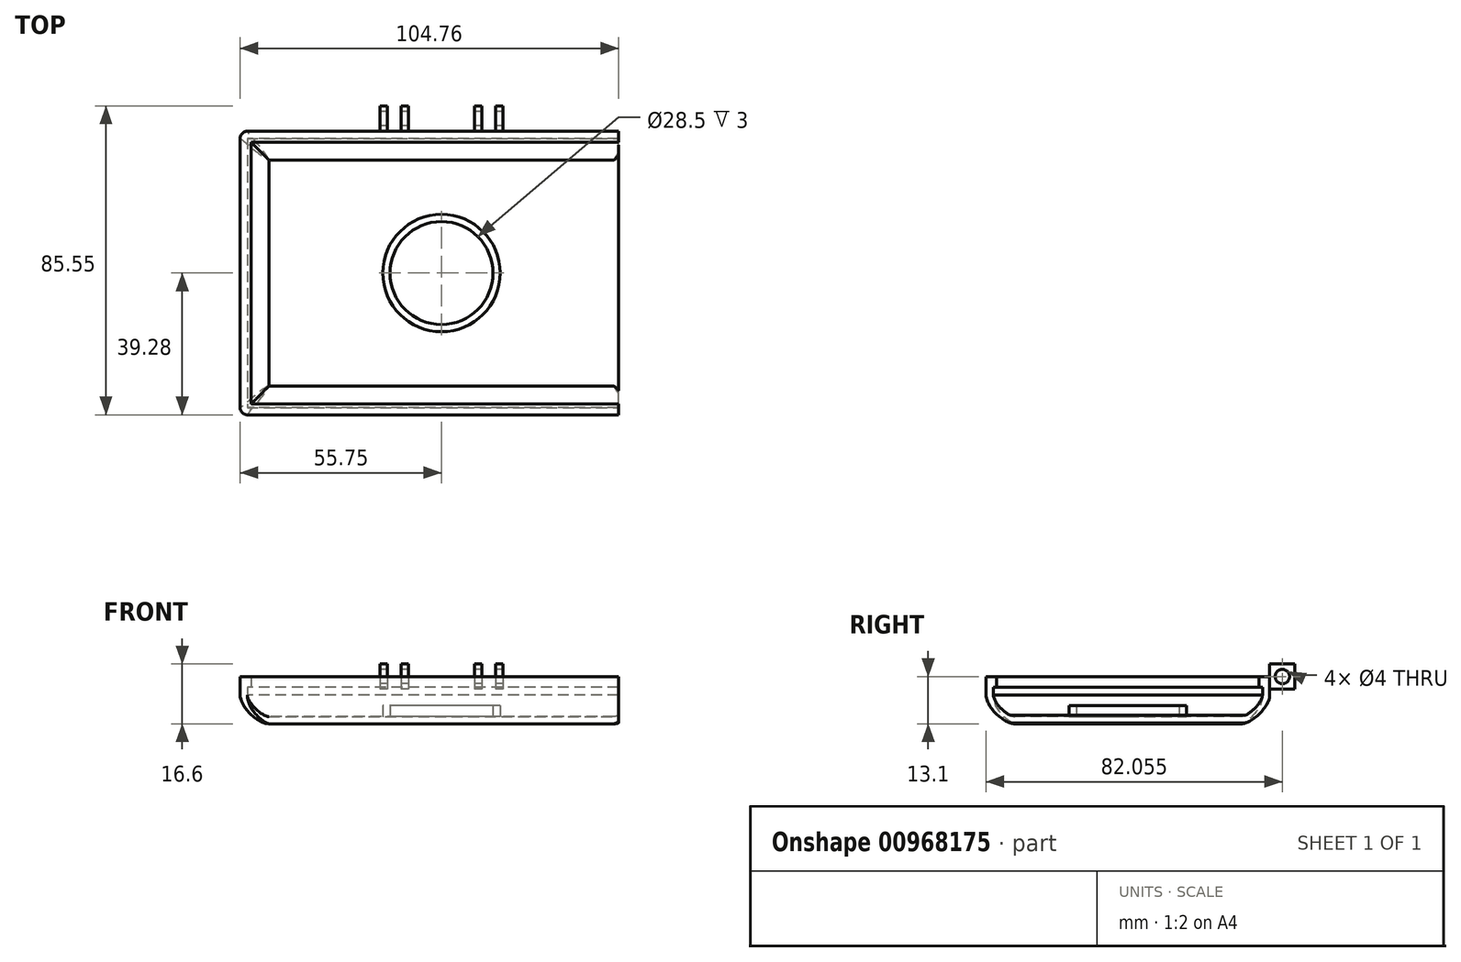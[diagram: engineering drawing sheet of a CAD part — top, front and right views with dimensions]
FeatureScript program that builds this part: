
annotation { "Feature Type Name" : "Feature", "Feature Type Description" : "" }
export const myFeature = defineFeature(function(context is Context, id is Id, definition is map)
    precondition{}
    {
        {
            var Q0;
            Q0=qCreatedBy(makeId("Top.planeOp"),FACE);
            var sketch = newSketch(context, id + "F0", { "sketchPlane" : qUnion([Q0])});
            skLineSegment(sketch, "E0.bottom", {"start": v(55.75, 39.28) * mm, "end": v(-55.75, 39.28) * mm});
            skLineSegment(sketch, "E0.top", {"start": v(55.75, -39.28) * mm, "end": v(-55.75, -39.28) * mm});
            skLineSegment(sketch, "E0.left", {"start": v(55.75, 39.28) * mm, "end": v(55.75, -39.28) * mm});
            skLineSegment(sketch, "E0.right", {"start": v(-55.75, 39.28) * mm, "end": v(-55.75, -39.28) * mm});
            skPoint(sketch, "E0.middle", {"position": v(0, 0) * mm});
            skSolve(sketch);
        }
        {
            var Q0;
            Q0=makeQuery(id+"F0.imprint","IMPRINT",FACE,{"disambiguationData":[TD([[makeQuery(id+"F0.imprint","IMPRINT",EDGE,{"derivedFrom":sQuery(id+"F0.wireOp",EDGE,"E0.bottom")}),1.0]])]});
            extrude(context, id + "F1", {"entities" : qUnion([Q0]), "oppositeDirection" : true, "depth" : 9.6 * mm, "offsetDistance" : 25 * mm});
        }
        {
            var Q0;
            Q0=makeQuery(id+"F1.opExtrude","CAP_FACE",FACE,{"disambiguationData":[OSD([sQuery(id+"F0.wireOp",EDGE,"E0.bottom"),sQuery(id+"F0.wireOp",EDGE,"E0.top"),sQuery(id+"F0.wireOp",EDGE,"E0.left"),sQuery(id+"F0.wireOp",EDGE,"E0.right")])],"isStart":false});
            fillet(context, id + "F2", {"entities" : qUnion([Q0]), "radius" : 8 * mm, "tangentPropagation" : true, "rho" : .3, "crossSection" : FilletCrossSection.CONIC, "allowEdgeOverflow" : false});
        }
        {
            var Q0;
            Q0=makeQuery(id+"F2.opFillet","BLEND_EDGE",EDGE,{"blendedFrom":[makeQuery(id+"F1.opExtrude","CAP_EDGE",EDGE,{"disambiguationData":[OSD([sQuery(id+"F0.wireOp",EDGE,"E0.top")])],"isStart":false}),makeQuery(id+"F1.opExtrude","CAP_EDGE",EDGE,{"disambiguationData":[OSD([sQuery(id+"F0.wireOp",EDGE,"E0.right")])],"isStart":false})],"blendedInto":[]});
            var Q1;
            Q1=makeQuery(id+"F2.opFillet","BLEND_EDGE",EDGE,{"blendedFrom":[makeQuery(id+"F1.opExtrude","CAP_EDGE",EDGE,{"disambiguationData":[OSD([sQuery(id+"F0.wireOp",EDGE,"E0.top")])],"isStart":false}),makeQuery(id+"F1.opExtrude","CAP_EDGE",EDGE,{"disambiguationData":[OSD([sQuery(id+"F0.wireOp",EDGE,"E0.left")])],"isStart":false})],"blendedInto":[]});
            var Q2;
            Q2=makeQuery(id+"F2.opFillet","BLEND_EDGE",EDGE,{"blendedFrom":[makeQuery(id+"F1.opExtrude","CAP_EDGE",EDGE,{"disambiguationData":[OSD([sQuery(id+"F0.wireOp",EDGE,"E0.bottom")])],"isStart":false}),makeQuery(id+"F1.opExtrude","CAP_EDGE",EDGE,{"disambiguationData":[OSD([sQuery(id+"F0.wireOp",EDGE,"E0.left")])],"isStart":false})],"blendedInto":[]});
            var Q3;
            Q3=makeQuery(id+"F2.opFillet","BLEND_EDGE",EDGE,{"blendedFrom":[makeQuery(id+"F1.opExtrude","CAP_EDGE",EDGE,{"disambiguationData":[OSD([sQuery(id+"F0.wireOp",EDGE,"E0.bottom")])],"isStart":false}),makeQuery(id+"F1.opExtrude","CAP_EDGE",EDGE,{"disambiguationData":[OSD([sQuery(id+"F0.wireOp",EDGE,"E0.right")])],"isStart":false})],"blendedInto":[]});
            fillet(context, id + "F3", {"entities" : qUnion([Q0, Q1, Q2, Q3]), "radius" : 2 * mm, "tangentPropagation" : true, "allowEdgeOverflow" : false});
        }
        {
            var Q0;
            Q0=makeQuery(id+"F1.opExtrude","CAP_FACE",FACE,{"disambiguationData":[OSD([sQuery(id+"F0.wireOp",EDGE,"E0.bottom"),sQuery(id+"F0.wireOp",EDGE,"E0.top"),sQuery(id+"F0.wireOp",EDGE,"E0.left"),sQuery(id+"F0.wireOp",EDGE,"E0.right")])],"isStart":true});
            shell(context, id + "F4", {"entities" : qUnion([Q0]), "thickness" : 2 * mm});
        }
        {
            var Q0;
            Q0=qCreatedBy(makeId("Top.planeOp"),FACE);
            var sketch = newSketch(context, id + "F5", { "sketchPlane" : qUnion([Q0])});
            skLineSegment(sketch, "E1.0", {"start": v(-53.75, 37.28) * mm, "end": v(-53.75, -37.28) * mm});
            skLineSegment(sketch, "E2.0", {"start": v(53.75, 37.28) * mm, "end": v(-53.75, 37.28) * mm});
            skLineSegment(sketch, "E3.0", {"start": v(53.75, 37.28) * mm, "end": v(53.75, -37.28) * mm});
            skLineSegment(sketch, "E4.0", {"start": v(53.75, -37.28) * mm, "end": v(-53.75, -37.28) * mm});
            skLineSegment(sketch, "E5.0", {"start": v(-55.75, 37.28) * mm, "end": v(-55.75, -37.28) * mm});
            skLineSegment(sketch, "E6.0.0", {"start": v(-53.75, -39.28) * mm, "end": v(53.75, -39.28) * mm});
            skArc(sketch, "E6.0.1", {"start": v(53.75, -39.28) * mm, "mid": v(55.16, -38.69) * mm, "end": v(55.75, -37.28) * mm});
            skLineSegment(sketch, "E6.0.2", {"start": v(55.75, -37.28) * mm, "end": v(55.75, 37.28) * mm});
            skArc(sketch, "E6.0.3", {"start": v(55.75, 37.28) * mm, "mid": v(55.16, 38.69) * mm, "end": v(53.75, 39.28) * mm});
            skLineSegment(sketch, "E6.0.4", {"start": v(53.75, 39.28) * mm, "end": v(-53.75, 39.28) * mm});
            skArc(sketch, "E6.0.5", {"start": v(-53.75, 39.28) * mm, "mid": v(-55.16, 38.69) * mm, "end": v(-55.75, 37.28) * mm});
            skArc(sketch, "E6.0.7", {"start": v(-55.75, -37.28) * mm, "mid": v(-55.16, -38.69) * mm, "end": v(-53.75, -39.28) * mm});
            skSolve(sketch);
        }
        {
            var Q0;
            Q0 = qSketchRegion(id + "F5", true);
            extrude(context, id + "F6", {"entities" : qUnion([Q0]), "operationType" : NewBodyOperationType.ADD, "depth" : .5 * mm, "offsetDistance" : 25 * mm});
        }
        {
            var Q0;
            Q0=makeQuery(id+"F6.opExtrude","CAP_FACE",FACE,{"disambiguationData":[OSD([sQuery(id+"F5.wireOp",EDGE,"E1.0"),sQuery(id+"F5.wireOp",EDGE,"E2.0"),sQuery(id+"F5.wireOp",EDGE,"E3.0"),sQuery(id+"F5.wireOp",EDGE,"E4.0"),sQuery(id+"F5.wireOp",EDGE,"E6.0.0"),sQuery(id+"F5.wireOp",EDGE,"E6.0.1"),sQuery(id+"F5.wireOp",EDGE,"E6.0.2"),sQuery(id+"F5.wireOp",EDGE,"E6.0.3"),sQuery(id+"F5.wireOp",EDGE,"E6.0.4"),sQuery(id+"F5.wireOp",EDGE,"E6.0.5"),sQuery(id+"F5.wireOp",EDGE,"E5.0"),sQuery(id+"F5.wireOp",EDGE,"E6.0.7")])],"isStart":false});
            var sketch = newSketch(context, id + "F7", { "sketchPlane" : qUnion([Q0])});
            skLineSegment(sketch, "E7.0", {"start": v(52.75, 36.27) * mm, "end": v(-52.75, 36.27) * mm});
            skLineSegment(sketch, "E7.1", {"start": v(52.75, 36.27) * mm, "end": v(52.75, -36.27) * mm});
            skLineSegment(sketch, "E7.2", {"start": v(52.75, -36.27) * mm, "end": v(-52.75, -36.27) * mm});
            skLineSegment(sketch, "E7.3", {"start": v(-52.75, 36.27) * mm, "end": v(-52.75, -36.27) * mm});
            skLineSegment(sketch, "E8.0", {"start": v(53.75, 39.28) * mm, "end": v(-53.75, 39.28) * mm});
            skPoint(sketch, "E9.0", {"position": v(55.16, 38.69) * mm});
            skArc(sketch, "E10.0", {"start": v(55.75, 37.28) * mm, "mid": v(55.16, 38.69) * mm, "end": v(53.75, 39.28) * mm});
            skLineSegment(sketch, "E11.0", {"start": v(55.75, -37.28) * mm, "end": v(55.75, 37.28) * mm});
            skArc(sketch, "E12.0", {"start": v(53.75, -39.28) * mm, "mid": v(55.16, -38.69) * mm, "end": v(55.75, -37.28) * mm});
            skLineSegment(sketch, "E13.0", {"start": v(-53.75, -39.28) * mm, "end": v(53.75, -39.28) * mm});
            skArc(sketch, "E14.0", {"start": v(-55.75, -37.28) * mm, "mid": v(-55.16, -38.69) * mm, "end": v(-53.75, -39.28) * mm});
            skLineSegment(sketch, "E15.0", {"start": v(-55.75, 37.28) * mm, "end": v(-55.75, -37.28) * mm});
            skArc(sketch, "E16.0", {"start": v(-53.75, 39.28) * mm, "mid": v(-55.16, 38.69) * mm, "end": v(-55.75, 37.28) * mm});
            skSolve(sketch);
        }
        {
            var Q0;
            Q0 = qSketchRegion(id + "F7", true);
            extrude(context, id + "F8", {"entities" : qUnion([Q0]), "operationType" : NewBodyOperationType.ADD, "depth" : 3 * mm, "offsetDistance" : 25 * mm});
        }
        {
            var Q0;
            Q0=makeQuery(id+"F4.opShell","OFFSET_FACE",FACE,{"disambiguationData":[OSD([sQuery(id+"F0.wireOp",EDGE,"E0.bottom"),sQuery(id+"F0.wireOp",EDGE,"E0.top"),sQuery(id+"F0.wireOp",EDGE,"E0.left"),sQuery(id+"F0.wireOp",EDGE,"E0.right")])]});
            var sketch = newSketch(context, id + "F9", { "sketchPlane" : qUnion([Q0])});
            skCircle(sketch, "E17", {"center": v(0, 0) * mm, "radius": 14.25 * mm});
            skCircle(sketch, "E18.0", {"center": v(0, 0) * mm, "radius": 16.25 * mm});
            skSolve(sketch);
        }
        {
            var Q0;
            Q0 = qSketchRegion(id + "F9", true);
            extrude(context, id + "F10", {"entities" : qUnion([Q0]), "operationType" : NewBodyOperationType.ADD, "depth" : 3 * mm, "offsetDistance" : 25 * mm});
        }
        {
            var Q0;
            Q0=qCreatedBy(makeId("Top.planeOp"),FACE);
            var sketch = newSketch(context, id + "F11", { "sketchPlane" : qUnion([Q0])});
            skLineSegment(sketch, "E19.bottom", {"start": v(49, 46.46) * mm, "end": v(61.97, 46.46) * mm});
            skLineSegment(sketch, "E19.top", {"start": v(49, -47.3) * mm, "end": v(61.97, -47.3) * mm});
            skLineSegment(sketch, "E19.left", {"start": v(49, 46.46) * mm, "end": v(49, -47.3) * mm});
            skLineSegment(sketch, "E19.right", {"start": v(61.97, 46.46) * mm, "end": v(61.97, -47.3) * mm});
            skSolve(sketch);
        }
        {
            var Q0;
            Q0 = qSketchRegion(id + "F11", true);
            extrude(context, id + "F12", {"entities" : qUnion([Q0]), "operationType" : NewBodyOperationType.REMOVE, "endBound" : BoundingType.SYMMETRIC, "oppositeDirection" : true, "depth" : 25 * mm, "offsetDistance" : 25 * mm});
        }
        {
            var Q0;
            Q0=makeQuery(id+"F8.opExtrude","CAP_FACE",FACE,{"disambiguationData":[OSD([sQuery(id+"F7.wireOp",EDGE,"E7.0"),sQuery(id+"F7.wireOp",EDGE,"E7.1"),sQuery(id+"F7.wireOp",EDGE,"E7.2"),sQuery(id+"F7.wireOp",EDGE,"E7.3"),sQuery(id+"F7.wireOp",EDGE,"E8.0"),sQuery(id+"F7.wireOp",EDGE,"E10.0"),sQuery(id+"F7.wireOp",EDGE,"E11.0"),sQuery(id+"F7.wireOp",EDGE,"E12.0"),sQuery(id+"F7.wireOp",EDGE,"E13.0"),sQuery(id+"F7.wireOp",EDGE,"E14.0"),sQuery(id+"F7.wireOp",EDGE,"E15.0"),sQuery(id+"F7.wireOp",EDGE,"E16.0")])],"isStart":false});
            var sketch = newSketch(context, id + "F13", { "sketchPlane" : qUnion([Q0])});
            skLineSegment(sketch, "E20.0", {"start": v(54.25, 39.28) * mm, "end": v(-53.75, 39.28) * mm, "construction": true});
            skLineSegment(sketch, "E21.bottom", {"start": v(-17, 39.28) * mm, "end": v(-15, 39.28) * mm});
            skLineSegment(sketch, "E21.top", {"start": v(-17, 46.27) * mm, "end": v(-15, 46.27) * mm});
            skLineSegment(sketch, "E21.left", {"start": v(-17, 39.28) * mm, "end": v(-17, 46.27) * mm});
            skLineSegment(sketch, "E21.right", {"start": v(-15, 39.28) * mm, "end": v(-15, 46.27) * mm});
            skLineSegment(sketch, "E22.1.0.0", {"start": v(-9.2, 39.28) * mm, "end": v(-9.2, 46.27) * mm});
            skLineSegment(sketch, "E22.1.0.1", {"start": v(-11.2, 46.27) * mm, "end": v(-9.2, 46.27) * mm});
            skLineSegment(sketch, "E22.1.0.2", {"start": v(-11.2, 39.28) * mm, "end": v(-9.2, 39.28) * mm});
            skLineSegment(sketch, "E22.1.0.3", {"start": v(-11.2, 39.28) * mm, "end": v(-11.2, 46.27) * mm});
            skLineSegment(sketch, "E22.direction1", {"start": v(-17, 39.28) * mm, "end": v(-11.2, 39.28) * mm, "construction": true});
            skLineSegment(sketch, "E23.MirrorCS", {"start": v(17, 39.28) * mm, "end": v(11.2, 39.28) * mm, "construction": true});
            skLineSegment(sketch, "E24.MirrorCS", {"start": v(-54.25, 39.28) * mm, "end": v(53.75, 39.28) * mm, "construction": true});
            skLineSegment(sketch, "E25.MirrorCS", {"start": v(17, 39.28) * mm, "end": v(15, 39.28) * mm});
            skLineSegment(sketch, "E26.MirrorCS", {"start": v(17, 46.27) * mm, "end": v(15, 46.27) * mm});
            skLineSegment(sketch, "E27.MirrorCS", {"start": v(9.2, 39.28) * mm, "end": v(9.2, 46.27) * mm});
            skLineSegment(sketch, "E28.MirrorCS", {"start": v(15, 39.28) * mm, "end": v(15, 46.27) * mm});
            skLineSegment(sketch, "E29.MirrorCS", {"start": v(11.2, 39.28) * mm, "end": v(11.2, 46.27) * mm});
            skLineSegment(sketch, "E30.MirrorCS", {"start": v(11.2, 39.28) * mm, "end": v(9.2, 39.28) * mm});
            skLineSegment(sketch, "E31.MirrorCS", {"start": v(11.2, 46.27) * mm, "end": v(9.2, 46.27) * mm});
            skLineSegment(sketch, "E32.MirrorCS", {"start": v(17, 39.28) * mm, "end": v(17, 46.27) * mm});
            skSolve(sketch);
        }
        {
            var Q0;
            Q0 = qSketchRegion(id + "F13", true);
            extrude(context, id + "F14", {"entities" : qUnion([Q0]), "operationType" : NewBodyOperationType.ADD, "endBound" : BoundingType.SYMMETRIC, "depth" : 7 * mm, "offsetDistance" : 25 * mm});
        }
        {
            var Q0;
            Q0=makeQuery(id+"F14.opExtrude","SWEPT_FACE",FACE,{"disambiguationData":[OSD([sQuery(id+"F13.wireOp",EDGE,"E21.left")])]});
            var sketch = newSketch(context, id + "F15", { "sketchPlane" : qUnion([Q0])});
            skCircle(sketch, "E33", {"center": v(-42.77, 3.5) * mm, "radius": 2 * mm});
            skPoint(sketch, "E34", {"position": v(-42.77, 7) * mm});
            skPoint(sketch, "E35", {"position": v(-46.27, 3.5) * mm});
            skSolve(sketch);
        }
        {
            var Q0;
            Q0 = qSketchRegion(id + "F15", true);
            extrude(context, id + "F16", {"entities" : qUnion([Q0]), "operationType" : NewBodyOperationType.REMOVE, "oppositeDirection" : true, "depth" : 80 * mm, "offsetDistance" : 25 * mm});
        }
    });
